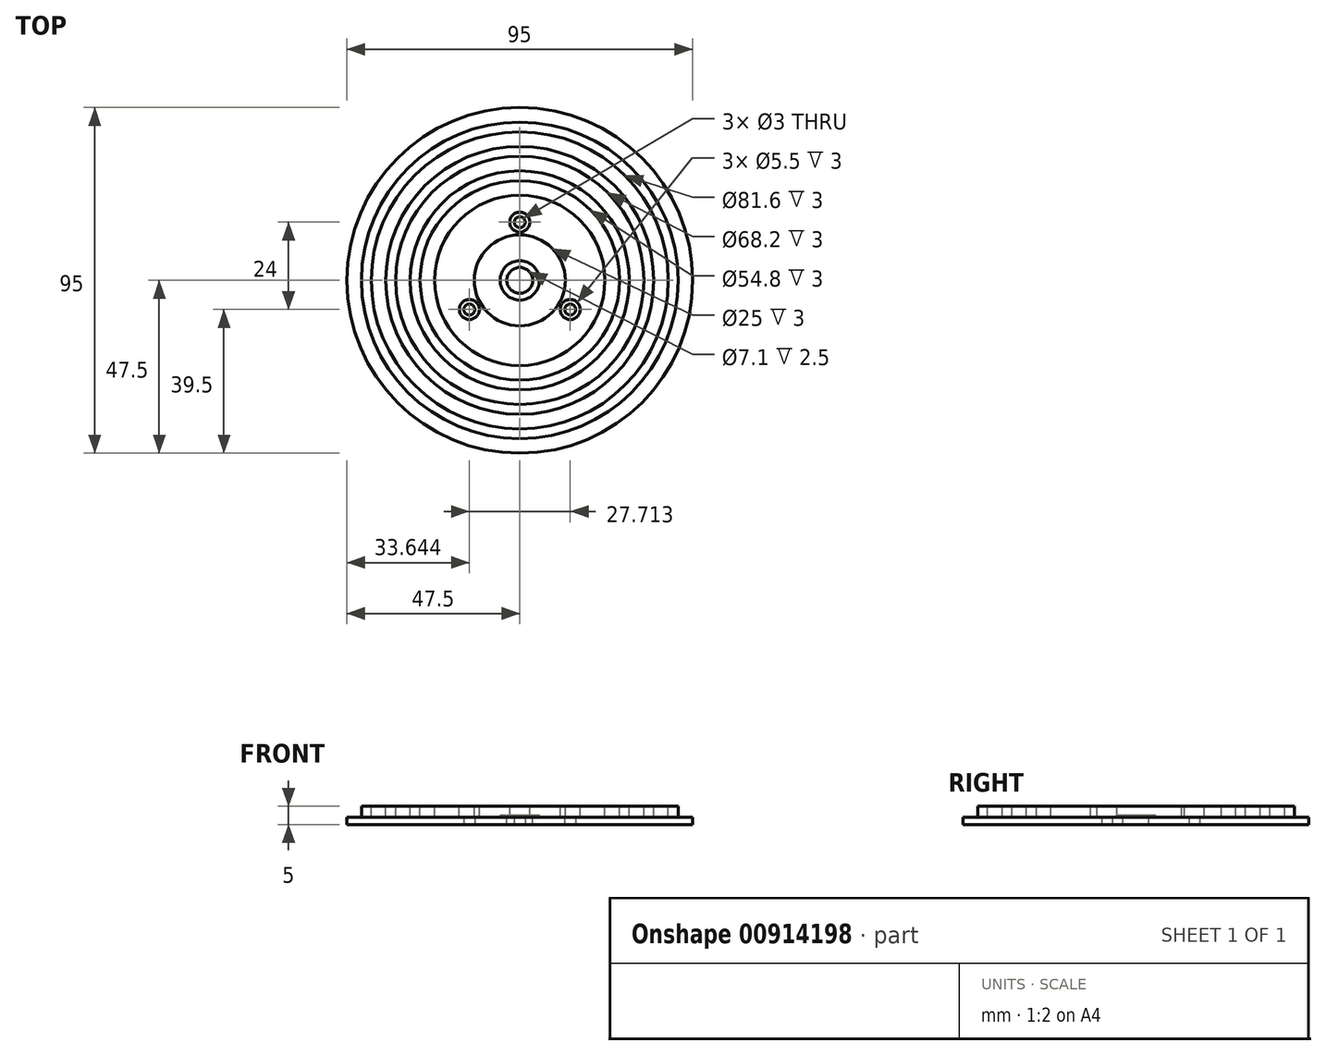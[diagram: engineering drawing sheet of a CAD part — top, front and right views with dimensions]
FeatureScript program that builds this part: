
annotation { "Feature Type Name" : "Feature", "Feature Type Description" : "" }
export const myFeature = defineFeature(function(context is Context, id is Id, definition is map)
    precondition{}
    {
        {
            var Q0;
            Q0=qCreatedBy(makeId("Front.planeOp"),FACE);
            var sketch = newSketch(context, id + "F0", { "sketchPlane" : qUnion([Q0])});
            skLineSegment(sketch, "E0", {"start": v(0, 9.24) * mm, "end": v(0, -8.58) * mm, "construction": true});
            skLineSegment(sketch, "E1", {"start": v(3.55, 0) * mm, "end": v(47.5, 0) * mm});
            skLineSegment(sketch, "E2", {"start": v(47.5, 0) * mm, "end": v(47.5, 2) * mm});
            skLineSegment(sketch, "E3", {"start": v(47.5, 2) * mm, "end": v(43.5, 2) * mm});
            skLineSegment(sketch, "E4", {"start": v(43.5, 2) * mm, "end": v(43.5, 5) * mm});
            skLineSegment(sketch, "E5", {"start": v(43.5, 5) * mm, "end": v(40.8, 5) * mm});
            skLineSegment(sketch, "E6", {"start": v(40.8, 5) * mm, "end": v(40.8, 2) * mm});
            skLineSegment(sketch, "E7", {"start": v(40.8, 2) * mm, "end": v(36.8, 2) * mm});
            skLineSegment(sketch, "E8", {"start": v(36.8, 2) * mm, "end": v(36.8, 5) * mm});
            skLineSegment(sketch, "E9", {"start": v(36.8, 5) * mm, "end": v(34.1, 5) * mm});
            skLineSegment(sketch, "E10", {"start": v(34.1, 5) * mm, "end": v(34.1, 2) * mm});
            skLineSegment(sketch, "E11", {"start": v(34.1, 2) * mm, "end": v(30.1, 2) * mm});
            skLineSegment(sketch, "E12", {"start": v(30.1, 2) * mm, "end": v(30.1, 5) * mm});
            skLineSegment(sketch, "E13", {"start": v(30.1, 5) * mm, "end": v(27.4, 5) * mm});
            skLineSegment(sketch, "E14", {"start": v(27.4, 5) * mm, "end": v(27.4, 2) * mm});
            skLineSegment(sketch, "E15", {"start": v(27.4, 2) * mm, "end": v(23.4, 2) * mm});
            skLineSegment(sketch, "E16", {"start": v(23.4, 2) * mm, "end": v(23.4, 5) * mm});
            skLineSegment(sketch, "E17", {"start": v(23.4, 5) * mm, "end": v(12.5, 5) * mm});
            skLineSegment(sketch, "E18", {"start": v(12.5, 5) * mm, "end": v(12.5, 2) * mm});
            skLineSegment(sketch, "E19", {"start": v(3.55, 2.5) * mm, "end": v(5.4, 2.5) * mm});
            skLineSegment(sketch, "E20", {"start": v(5.4, 2.5) * mm, "end": v(5.4, 2) * mm});
            skLineSegment(sketch, "E21", {"start": v(5.4, 2) * mm, "end": v(12.5, 2) * mm});
            skLineSegment(sketch, "E22", {"start": v(3.55, 2.5) * mm, "end": v(3.55, 0) * mm});
            skSolve(sketch);
        }
        {
            var Q0;
            Q0=qSketchRegion(id+"F0",true);
            var Q1;
            Q1=sQuery(id+"F0.wireOp",EDGE,"E0");
            revolve(context, id + "F1", {"surfaceOperationType" : NewSurfaceOperationType.NEW, "entities" : qUnion([Q0]), "axis" : qUnion([Q1]), "revolveType" : RevolveType.FULL});
        }
        {
            var Q0;
            Q0=qCreatedBy(makeId("Top.planeOp"),FACE);
            var sketch = newSketch(context, id + "F2", { "sketchPlane" : qUnion([Q0])});
            skCircle(sketch, "E23", {"center": v(0, 16) * mm, "radius": 1.5 * mm});
            skCircle(sketch, "E24.1.0", {"center": v(-13.86, -8) * mm, "radius": 1.5 * mm});
            skCircle(sketch, "E24.2.0", {"center": v(13.86, -8) * mm, "radius": 1.5 * mm});
            skPoint(sketch, "E24.center", {"position": v(0, 0) * mm});
            skSolve(sketch);
        }
        {
            var Q0;
            Q0=qSketchRegion(id+"F2",true);
            extrude(context, id + "F3", {"entities" : qUnion([Q0]), "operationType" : NewBodyOperationType.REMOVE, "endBound" : BoundingType.THROUGH_ALL, "depth" : 25 * mm, "offsetDistance" : 25 * mm});
        }
        {
            var Q0;
            Q0=makeQuery(id+"F1.opRevolve","SWEPT_FACE",FACE,{"disambiguationData":[OSD([sQuery(id+"F0.wireOp",EDGE,"E17")])]});
            var sketch = newSketch(context, id + "F4", { "sketchPlane" : qUnion([Q0])});
            skCircle(sketch, "E25", {"center": v(0, 16) * mm, "radius": 2.75 * mm});
            skCircle(sketch, "E26.1.0", {"center": v(-13.86, -8) * mm, "radius": 2.75 * mm});
            skCircle(sketch, "E26.2.0", {"center": v(13.86, -8) * mm, "radius": 2.75 * mm});
            skPoint(sketch, "E26.center", {"position": v(0, 0) * mm});
            skSolve(sketch);
        }
        {
            var Q0;
            Q0 = qSketchRegion(id + "F4", true);
            extrude(context, id + "F5", {"entities" : qUnion([Q0]), "operationType" : NewBodyOperationType.REMOVE, "oppositeDirection" : true, "depth" : 3 * mm, "offsetDistance" : 25 * mm});
        }
    });
